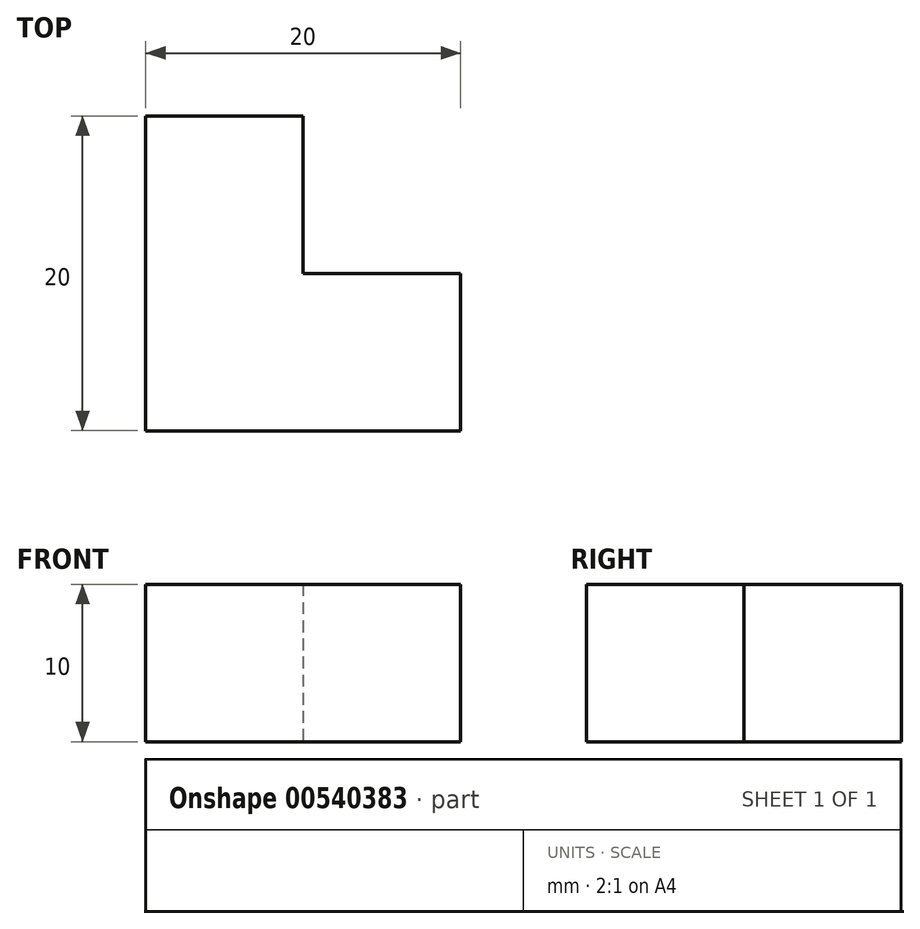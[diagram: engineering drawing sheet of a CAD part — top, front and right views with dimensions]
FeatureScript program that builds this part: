
annotation { "Feature Type Name" : "Feature", "Feature Type Description" : "" }
export const myFeature = defineFeature(function(context is Context, id is Id, definition is map)
    precondition{}
    {
        {
            var Q0;
            Q0=qCreatedBy(makeId("Top.planeOp"),FACE);
            var sketch = newSketch(context, id + "F0", { "sketchPlane" : qUnion([Q0])});
            skLineSegment(sketch, "E0", {"start": v(-73.08, 24) * mm, "end": v(-73.08, 4) * mm});
            skLineSegment(sketch, "E1", {"start": v(-73.08, 4) * mm, "end": v(-53.08, 4) * mm});
            skLineSegment(sketch, "E2", {"start": v(-73.08, 24) * mm, "end": v(-63.08, 24) * mm});
            skLineSegment(sketch, "E3", {"start": v(-63.08, 24) * mm, "end": v(-63.08, 14) * mm});
            skLineSegment(sketch, "E4", {"start": v(-53.08, 4) * mm, "end": v(-53.08, 14) * mm});
            skPoint(sketch, "E5.start.orphan", {"position": v(-63.08, 13.26) * mm});
            skLineSegment(sketch, "E6", {"start": v(-63.08, 14) * mm, "end": v(-53.08, 14) * mm});
            skSolve(sketch);
        }
        {
            var Q0;
            Q0=makeQuery(id+"F0.imprint","IMPRINT",FACE,{"disambiguationData":[TD([[makeQuery(id+"F0.imprint","IMPRINT",EDGE,{"derivedFrom":sQuery(id+"F0.wireOp",EDGE,"E0")}),1.0]])]});
            extrude(context, id + "F1", {"entities" : qUnion([Q0]), "depth" : 10 * mm, "offsetDistance" : 25 * mm});
        }
    });
